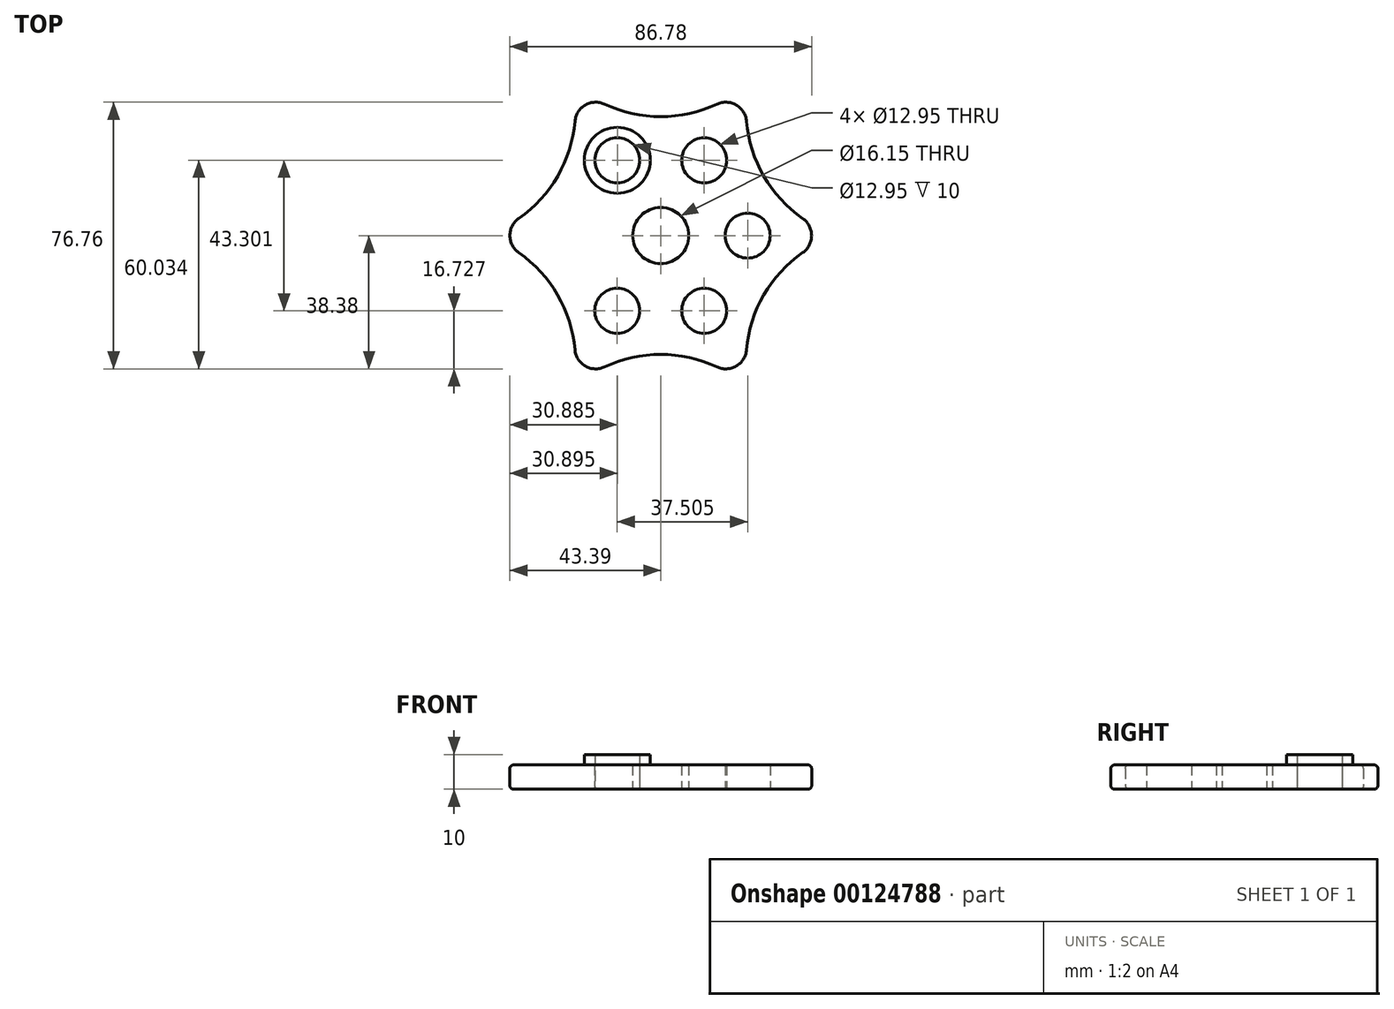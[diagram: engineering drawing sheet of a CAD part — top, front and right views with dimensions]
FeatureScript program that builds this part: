
annotation { "Feature Type Name" : "Feature", "Feature Type Description" : "" }
export const myFeature = defineFeature(function(context is Context, id is Id, definition is map)
    precondition{}
    {
        {
            var Q0;
            Q0=qCreatedBy(makeId("Top.planeOp"),FACE);
            var sketch = newSketch(context, id + "F0", { "sketchPlane" : qUnion([Q0])});
            skCircle(sketch, "E0.cCircle", {"center": v(0, 0) * mm, "radius": 43.85 * mm, "construction": true});
            skLineSegment(sketch, "E0.0", {"start": v(-25.33, -43.84) * mm, "end": v(-50.63, 0.01) * mm});
            skLineSegment(sketch, "E0.1", {"start": v(-50.63, 0.01) * mm, "end": v(-25.3, 43.85) * mm});
            skLineSegment(sketch, "E0.2", {"start": v(-25.3, 43.85) * mm, "end": v(25.33, 43.84) * mm});
            skLineSegment(sketch, "E0.3", {"start": v(25.33, 43.84) * mm, "end": v(50.63, -0.01) * mm});
            skLineSegment(sketch, "E0.4", {"start": v(50.63, -0.01) * mm, "end": v(25.3, -43.85) * mm});
            skLineSegment(sketch, "E0.5", {"start": v(25.3, -43.85) * mm, "end": v(-25.33, -43.84) * mm});
            skPoint(sketch, "E0.0.midPoint", {"position": v(-37.98, -21.92) * mm});
            skArc(sketch, "E1", {"start": v(-16.14, 37.82) * mm, "mid": v(0, 34.22) * mm, "end": v(16.16, 37.81) * mm});
            skArc(sketch, "E2", {"start": v(24.68, 32.89) * mm, "mid": v(29.64, 17.1) * mm, "end": v(40.82, 4.91) * mm});
            skArc(sketch, "E3", {"start": v(40.82, -4.93) * mm, "mid": v(29.63, -17.12) * mm, "end": v(24.66, -32.9) * mm});
            skArc(sketch, "E4", {"start": v(16.14, -37.82) * mm, "mid": v(0, -34.22) * mm, "end": v(-16.16, -37.81) * mm});
            skArc(sketch, "E5", {"start": v(-24.68, -32.89) * mm, "mid": v(-29.64, -17.1) * mm, "end": v(-40.82, -4.91) * mm});
            skArc(sketch, "E6", {"start": v(-40.82, 4.93) * mm, "mid": v(-29.63, 17.12) * mm, "end": v(-24.66, 32.9) * mm});
            skPoint(sketch, "E7.visualSharp", {"position": v(-25.3, 43.85) * mm});
            skArc(sketch, "E7.filletArc", {"start": v(-16.14, 37.82) * mm, "mid": v(-21.69, 37.58) * mm, "end": v(-24.66, 32.9) * mm});
            skPoint(sketch, "E8.visualSharp", {"position": v(25.33, 43.84) * mm});
            skArc(sketch, "E8.filletArc", {"start": v(24.68, 32.89) * mm, "mid": v(21.7, 37.57) * mm, "end": v(16.16, 37.81) * mm});
            skPoint(sketch, "E9.visualSharp", {"position": v(50.63, -0.01) * mm});
            skArc(sketch, "E9.filletArc", {"start": v(40.82, -4.93) * mm, "mid": v(43.39, 0) * mm, "end": v(40.82, 4.91) * mm});
            skPoint(sketch, "E10.visualSharp", {"position": v(25.3, -43.85) * mm});
            skArc(sketch, "E10.filletArc", {"start": v(16.14, -37.82) * mm, "mid": v(21.69, -37.58) * mm, "end": v(24.66, -32.9) * mm});
            skPoint(sketch, "E11.visualSharp", {"position": v(-25.33, -43.84) * mm});
            skArc(sketch, "E11.filletArc", {"start": v(-24.68, -32.89) * mm, "mid": v(-21.7, -37.57) * mm, "end": v(-16.16, -37.81) * mm});
            skPoint(sketch, "E12.visualSharp", {"position": v(-50.63, 0.01) * mm});
            skArc(sketch, "E12.filletArc", {"start": v(-40.82, 4.93) * mm, "mid": v(-43.39, 0) * mm, "end": v(-40.82, -4.91) * mm});
            skCircle(sketch, "E13", {"center": v(-12.5, 21.65) * mm, "radius": 6.47 * mm});
            skCircle(sketch, "E14", {"center": v(12.5, 21.65) * mm, "radius": 6.47 * mm});
            skCircle(sketch, "E15", {"center": v(25, 0) * mm, "radius": 6.47 * mm});
            skCircle(sketch, "E16", {"center": v(12.5, -21.65) * mm, "radius": 6.47 * mm});
            skCircle(sketch, "E17", {"center": v(-12.5, -21.65) * mm, "radius": 6.47 * mm});
            skCircle(sketch, "E18", {"center": v(-59, 20.32) * mm, "radius": 6.47 * mm});
            skCircle(sketch, "E19", {"center": v(0, 0) * mm, "radius": 8.07 * mm});
            skCircle(sketch, "E20", {"center": v(-12.5, 21.65) * mm, "radius": 9.49 * mm});
            skSolve(sketch);
        }
        {
            var Q0;
            Q0=makeQuery(id+"F0.imprint","IMPRINT",FACE,{"disambiguationData":[TD([[makeQuery(id+"F0.imprint","IMPRINT",EDGE,{"derivedFrom":sQuery(id+"F0.wireOp",EDGE,"E1")}),-1.0]])]});
            extrude(context, id + "F1", {"entities" : qUnion([Q0]), "depth" : 7 * mm});
        }
        {
            var Q0;
            Q0=makeQuery(id+"F1.opExtrude","CAP_EDGE",EDGE,{"disambiguationData":[OSD([sQuery(id+"F0.wireOp",EDGE,"E1")])],"isStart":false});
            var Q1;
            Q1=makeQuery(id+"F1.opExtrude","CAP_EDGE",EDGE,{"disambiguationData":[OSD([sQuery(id+"F0.wireOp",EDGE,"E6")])],"isStart":true});
            fillet(context, id + "F2", {"entities" : qUnion([Q0, Q1]), "radius" : 1 * mm, "tangentPropagation" : true, "allowEdgeOverflow" : false});
        }
        {
            var Q0;
            Q0=makeQuery(id+"F0.imprint","IMPRINT",FACE,{"disambiguationData":[TD([[makeQuery(id+"F0.imprint","IMPRINT",EDGE,{"derivedFrom":sQuery(id+"F0.wireOp",EDGE,"E13")}),-1.0]])]});
            extrude(context, id + "F3", {"entities" : qUnion([Q0]), "operationType" : NewBodyOperationType.ADD, "depth" : 10 * mm});
        }
    });
